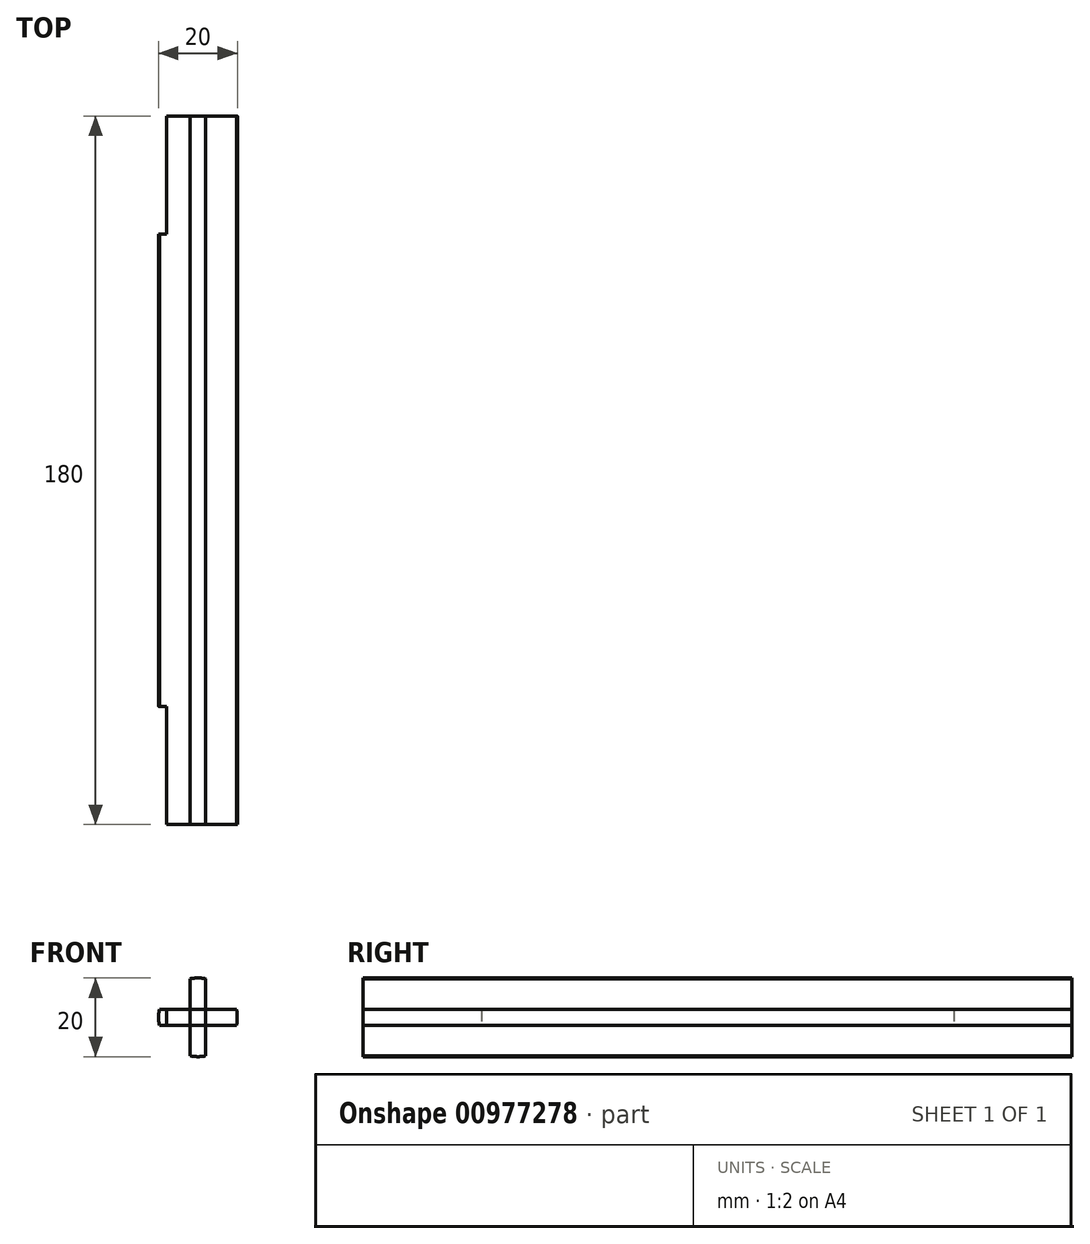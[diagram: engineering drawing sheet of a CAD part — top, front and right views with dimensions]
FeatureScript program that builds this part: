
annotation { "Feature Type Name" : "Feature", "Feature Type Description" : "" }
export const myFeature = defineFeature(function(context is Context, id is Id, definition is map)
    precondition{}
    {
        {
            var Q0;
            Q0=qCreatedBy(makeId("Front.planeOp"),FACE);
            var sketch = newSketch(context, id + "F0", { "sketchPlane" : qUnion([Q0])});
            skCircle(sketch, "E0", {"center": v(0, 0) * mm, "radius": 10 * mm});
            skLineSegment(sketch, "E1.bottom", {"start": v(-2, 12.5) * mm, "end": v(2, 12.5) * mm});
            skLineSegment(sketch, "E1.top", {"start": v(-2, -12.5) * mm, "end": v(2, -12.5) * mm});
            skLineSegment(sketch, "E1.left", {"start": v(-2, 12.5) * mm, "end": v(-2, -12.5) * mm});
            skLineSegment(sketch, "E1.right", {"start": v(2, 12.5) * mm, "end": v(2, -12.5) * mm});
            skLineSegment(sketch, "E2.bottom", {"start": v(12.5, -2) * mm, "end": v(-12.5, -2) * mm});
            skLineSegment(sketch, "E2.top", {"start": v(12.5, 2) * mm, "end": v(-12.5, 2) * mm});
            skLineSegment(sketch, "E2.left", {"start": v(12.5, -2) * mm, "end": v(12.5, 2) * mm});
            skLineSegment(sketch, "E2.right", {"start": v(-12.5, -2) * mm, "end": v(-12.5, 2) * mm});
            skLineSegment(sketch, "E3.bottom", {"start": v(-2, 8) * mm, "end": v(2, 8) * mm});
            skLineSegment(sketch, "E3.top", {"start": v(-2, -8) * mm, "end": v(2, -8) * mm});
            skLineSegment(sketch, "E3.left", {"start": v(-2, 8) * mm, "end": v(-2, -8) * mm});
            skLineSegment(sketch, "E3.right", {"start": v(2, 8) * mm, "end": v(2, -8) * mm});
            skLineSegment(sketch, "E4.bottom", {"start": v(8, 2) * mm, "end": v(-8, 2) * mm});
            skLineSegment(sketch, "E4.top", {"start": v(8, -2) * mm, "end": v(-8, -2) * mm});
            skLineSegment(sketch, "E4.left", {"start": v(8, 2) * mm, "end": v(8, -2) * mm});
            skLineSegment(sketch, "E4.right", {"start": v(-8, 2) * mm, "end": v(-8, -2) * mm});
            skSolve(sketch);
        }
        {
            var Q0;
            {var subQ0=sQuery(id+"F0.wireOp",EDGE,"E3.bottom");Q0=makeQuery(id+"F0.imprint","IMPRINT",FACE,{"disambiguationData":[TD([[makeQuery(id+"F0.imprint","IMPRINT",EDGE,{"derivedFrom":subQ0}),-1.0]])]});}
            var Q1;
            {var subQ1=sQuery(id+"F0.wireOp",EDGE,"E1.right");var subQ5=sQuery(id+"F0.wireOp",EDGE,"E0");var subQ6=makeQuery(id+"F0.imprint","INTERSECT",VERTEX,{"disambiguationData":[OD(0.0)],"derivedFrom":[subQ5,subQ1]});Q1=makeQuery(id+"F0.imprint","IMPRINT",FACE,{"disambiguationData":[TD([[makeQuery(id+"F0.imprint","IMPRINT",EDGE,{"disambiguationData":[TD([[subQ6,1.0]])],"derivedFrom":subQ5}),1.0]])]});}
            var Q2;
            {var subQ5=sQuery(id+"F0.wireOp",EDGE,"E4.left");Q2=makeQuery(id+"F0.imprint","IMPRINT",FACE,{"disambiguationData":[TD([[makeQuery(id+"F0.imprint","IMPRINT",EDGE,{"derivedFrom":subQ5}),-1.0]])]});}
            var Q3;
            {var subQ1=sQuery(id+"F0.wireOp",EDGE,"E1.right");var subQ7=sQuery(id+"F0.wireOp",EDGE,"E0");var subQ9=makeQuery(id+"F0.imprint","INTERSECT",VERTEX,{"disambiguationData":[OD(1.0)],"derivedFrom":[subQ7,subQ1]});Q3=makeQuery(id+"F0.imprint","IMPRINT",FACE,{"disambiguationData":[TD([[makeQuery(id+"F0.imprint","IMPRINT",EDGE,{"disambiguationData":[TD([[subQ9,-1.0]])],"derivedFrom":subQ7}),1.0]])]});}
            var Q4;
            {var subQ0=sQuery(id+"F0.wireOp",EDGE,"E3.top");Q4=makeQuery(id+"F0.imprint","IMPRINT",FACE,{"disambiguationData":[TD([[makeQuery(id+"F0.imprint","IMPRINT",EDGE,{"derivedFrom":subQ0}),1.0]])]});}
            var Q5;
            {var subQ5=sQuery(id+"F0.wireOp",EDGE,"E4.right");Q5=makeQuery(id+"F0.imprint","IMPRINT",FACE,{"disambiguationData":[TD([[makeQuery(id+"F0.imprint","IMPRINT",EDGE,{"derivedFrom":subQ5}),1.0]])]});}
            var Q6;
            {var subQ0=sQuery(id+"F0.wireOp",EDGE,"E4.bottom");var subQ1=sQuery(id+"F0.wireOp",EDGE,"E3.left");var subQ2=makeQuery(id+"F0.imprint","INTERSECT",VERTEX,{"derivedFrom":[subQ1,subQ0]});Q6=makeQuery(id+"F0.imprint","IMPRINT",FACE,{"disambiguationData":[TD([[makeQuery(id+"F0.imprint","IMPRINT",EDGE,{"disambiguationData":[TD([[subQ2,-1.0]])],"derivedFrom":subQ1}),1.0]])]});}
            var Q7;
            {var subQ1=sQuery(id+"F0.wireOp",EDGE,"E1.left");var subQ7=sQuery(id+"F0.wireOp",EDGE,"E0");var subQ9=makeQuery(id+"F0.imprint","INTERSECT",VERTEX,{"disambiguationData":[OD(0.0)],"derivedFrom":[subQ7,subQ1]});Q7=makeQuery(id+"F0.imprint","IMPRINT",FACE,{"disambiguationData":[TD([[makeQuery(id+"F0.imprint","IMPRINT",EDGE,{"disambiguationData":[TD([[subQ9,-1.0]])],"derivedFrom":subQ7}),1.0]])]});}
            var Q8;
            {var subQ1=sQuery(id+"F0.wireOp",EDGE,"E2.bottom");var subQ3=sQuery(id+"F0.wireOp",EDGE,"E0");var subQ4=makeQuery(id+"F0.imprint","INTERSECT",VERTEX,{"disambiguationData":[OD(0.0)],"derivedFrom":[subQ3,subQ1]});Q8=makeQuery(id+"F0.imprint","IMPRINT",FACE,{"disambiguationData":[TD([[makeQuery(id+"F0.imprint","IMPRINT",EDGE,{"disambiguationData":[TD([[subQ4,-1.0]])],"derivedFrom":subQ3}),1.0]])]});}
            extrude(context, id + "F1", {"entities" : qUnion([Q0, Q1, Q2, Q3, Q4, Q5, Q6, Q7, Q8]), "depth" : 180 * mm, "offsetDistance" : 25 * mm});
        }
        {
            var Q0;
            {var subQ5=sQuery(id+"F0.wireOp",EDGE,"E3.bottom");Q0=makeQuery(id+"F0.imprint","IMPRINT",FACE,{"disambiguationData":[TD([[makeQuery(id+"F0.imprint","IMPRINT",EDGE,{"derivedFrom":subQ5}),1.0]])]});}
            var Q1;
            {var subQ5=sQuery(id+"F0.wireOp",EDGE,"E4.right");Q1=makeQuery(id+"F0.imprint","IMPRINT",FACE,{"disambiguationData":[TD([[makeQuery(id+"F0.imprint","IMPRINT",EDGE,{"derivedFrom":subQ5}),-1.0]])]});}
            var Q2;
            {var subQ5=sQuery(id+"F0.wireOp",EDGE,"E3.top");Q2=makeQuery(id+"F0.imprint","IMPRINT",FACE,{"disambiguationData":[TD([[makeQuery(id+"F0.imprint","IMPRINT",EDGE,{"derivedFrom":subQ5}),-1.0]])]});}
            var Q3;
            {var subQ5=sQuery(id+"F0.wireOp",EDGE,"E4.left");Q3=makeQuery(id+"F0.imprint","IMPRINT",FACE,{"disambiguationData":[TD([[makeQuery(id+"F0.imprint","IMPRINT",EDGE,{"derivedFrom":subQ5}),1.0]])]});}
            extrude(context, id + "F2", {"entities" : qUnion([Q0, Q1, Q2, Q3]), "operationType" : NewBodyOperationType.ADD, "depth" : 150 * mm, "offsetDistance" : 25 * mm, "hasSecondDirection" : true, "secondDirectionOppositeDirection" : false, "secondDirectionDepth" : 30 * mm});
        }
    });
